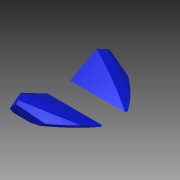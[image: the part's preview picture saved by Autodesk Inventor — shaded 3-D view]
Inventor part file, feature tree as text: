
AUTODESK INVENTOR PART (.ipt)
format: ipt  version: 2016 (Build 200138000, 138)  size: 223,232 bytes
history: native  units: in
note: dims shown in document units (in); Inventor stores cm internally (conversion verified against a paired STEP export)
features: sketch x3, plane x1, loft x1, extrude x1, chamfer x1
ambient origin geometry x8: Origin, YZ Plane, XZ Plane, XY Plane, X Axis, Y Axis, Z Axis, Center Point
bodies: Solid1 (feature_tree)
feature tree (7):
  sketch  "Sketch1"  dims[d0=0.7559in d1=0.7559in]
  plane  "Work Plane1"
  loft  "Main Body"
  extrude  "Create Eyes"  Depth=0.2in
  chamfer  "Eyes Chamfer"  Distance=0.08in
  sketch  "Sketch2"  dims[d2=0.9963in d3=0.2in]
  sketch  "Sketch3"  dims[d4=0.5in d6=0.08in d7=0.55in d8=150.0deg d9=150.0deg d14=0.33in d15=0.66in d18=0.0in d19=90.0deg d20=0.0in d21=90.0deg d22=1.0in d26=1.0651in d28=1.0651in d29=0.0in d30=0.962in d31=0.962in d32=0.075in d33=0.15in d34=0.06in d35=0.1in d36=0.05in d37=0.45in d38=0.0in d125=0.02in d126=0.125in d127=45.0deg]
